FCSTD DOCUMENT  (FreeCAD 0.16R6712 (Git))
Label: head_platform_v1
License: All rights reserved
LicenseURL: http://en.wikipedia.org/wiki/All_rights_reserved
objects: App::DocumentObjectGroup×3, Mesh::Feature×1, Sketcher::SketchObject×1
note: 1 computed .brp shape members not serialized (recipe doc carries the construction recipe); baked Part::Feature solids carry a one-line shape summary decoded from their .brp

FEATURE [Mesh::Feature] platform
FEATURE [App::DocumentObjectGroup] Group  label="External"
  Group = -> [platform]
FEATURE [Sketcher::SketchObject] Sketch
  sketch-geometry (9):
    g0: LineSegment StartX=0 StartY=65.8179 StartZ=0 EndX=-57 EndY=-32.909 EndZ=0
    g1: LineSegment StartX=-57 StartY=-32.909 StartZ=0 EndX=57 EndY=-32.909 EndZ=0
    g2: LineSegment StartX=57 StartY=-32.909 StartZ=0 EndX=0 EndY=65.8179 EndZ=0
    g3: Circle [constr] CenterX=0 CenterY=0 CenterZ=0 NormalX=0 NormalY=0 NormalZ=1 Radius=65.8179
    g4: GeomPoint [constr] X=-28.5 Y=16.4545 Z=0
    g5: GeomPoint [constr] X=-41 Y=-5.19615 Z=0
    g6: GeomPoint [constr] X=-16 Y=38.1051 Z=0
    g7: Circle CenterX=-16 CenterY=38.1051 CenterZ=0 NormalX=0 NormalY=0 NormalZ=1 Radius=6
    g8: Circle CenterX=-41 CenterY=-5.19615 CenterZ=0 NormalX=0 NormalY=0 NormalZ=1 Radius=6
  constraints (20):
    c: Coincident(g0,g1)
    c: Coincident(g1,g2)
    c: Coincident(g2,g0)
    c: Equal(g0,g1)
    c: Equal(g0,g2)
    c: PointOnObject(g0,g3)
    c: PointOnObject(g1,g3)
    c: PointOnObject(g2,g3)
    c: Coincident(g3,g-1)
    c: PointOnObject(g0,g-2)
    c: Distance(g0) = 114
    c: PointOnObject(g5,g0)
    c: PointOnObject(g6,g0)
    c: Symmetric(g0,g0,g4)
    c: Symmetric(g5,g6,g4)
    c: Distance(g5,g6) = 50
    c: Coincident(g7,g6)
    c: Coincident(g8,g5)
    c: Equal(g8,g7)
    c: Radius(g8) = 6
FEATURE [App::DocumentObjectGroup] Group001  label="Helpers"
  Group = -> [Sketch]
FEATURE [App::DocumentObjectGroup] Group002  label="Documents"
